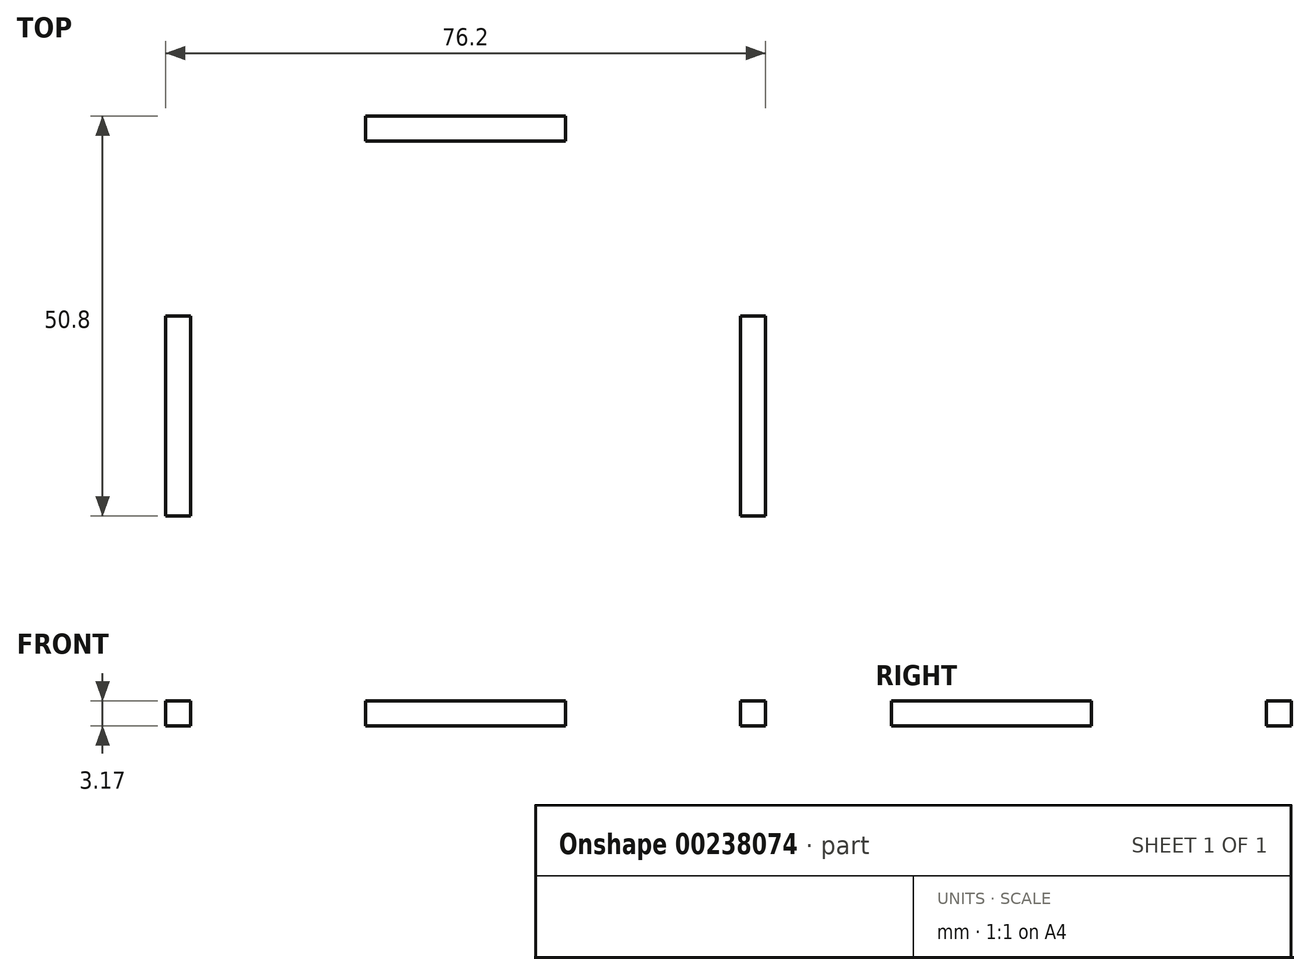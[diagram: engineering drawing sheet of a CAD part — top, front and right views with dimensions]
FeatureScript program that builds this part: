
annotation { "Feature Type Name" : "Feature", "Feature Type Description" : "" }
export const myFeature = defineFeature(function(context is Context, id is Id, definition is map)
    precondition{}
    {
        {
            var Q0;
            Q0=qCreatedBy(makeId("Top.planeOp"),FACE);
            var sketch = newSketch(context, id + "F0", { "sketchPlane" : qUnion([Q0])});
            skLineSegment(sketch, "E0.bottom", {"start": v(34.93, -34.93) * mm, "end": v(-34.93, -34.93) * mm});
            skLineSegment(sketch, "E0.top", {"start": v(34.93, 34.93) * mm, "end": v(-34.93, 34.93) * mm});
            skLineSegment(sketch, "E0.left", {"start": v(34.93, -34.93) * mm, "end": v(34.93, 34.92) * mm});
            skLineSegment(sketch, "E0.right", {"start": v(-34.93, -34.93) * mm, "end": v(-34.93, 34.92) * mm});
            skPoint(sketch, "E0.middle", {"position": v(0, 0) * mm});
            skLineSegment(sketch, "E1.bottom", {"start": v(-12.7, 38.1) * mm, "end": v(12.7, 38.1) * mm});
            skLineSegment(sketch, "E1.top", {"start": v(-12.7, 34.92) * mm, "end": v(12.7, 34.92) * mm});
            skLineSegment(sketch, "E1.left", {"start": v(-12.7, 38.1) * mm, "end": v(-12.7, 34.92) * mm});
            skLineSegment(sketch, "E1.right", {"start": v(12.7, 38.1) * mm, "end": v(12.7, 34.92) * mm});
            skLineSegment(sketch, "E2.bottom", {"start": v(-12.7, -34.93) * mm, "end": v(12.7, -34.93) * mm});
            skLineSegment(sketch, "E2.top", {"start": v(-12.7, -38.1) * mm, "end": v(12.7, -38.1) * mm});
            skLineSegment(sketch, "E2.left", {"start": v(-12.7, -34.93) * mm, "end": v(-12.7, -38.1) * mm});
            skLineSegment(sketch, "E2.right", {"start": v(12.7, -34.93) * mm, "end": v(12.7, -38.1) * mm});
            skLineSegment(sketch, "E3.bottom", {"start": v(34.93, 12.7) * mm, "end": v(38.1, 12.7) * mm});
            skLineSegment(sketch, "E3.top", {"start": v(34.93, -12.7) * mm, "end": v(38.1, -12.7) * mm});
            skLineSegment(sketch, "E3.left", {"start": v(34.93, 12.7) * mm, "end": v(34.93, -12.7) * mm});
            skLineSegment(sketch, "E3.right", {"start": v(38.1, 12.7) * mm, "end": v(38.1, -12.7) * mm});
            skLineSegment(sketch, "E4.bottom", {"start": v(-38.1, 12.7) * mm, "end": v(-34.93, 12.7) * mm});
            skLineSegment(sketch, "E4.top", {"start": v(-38.1, -12.7) * mm, "end": v(-34.93, -12.7) * mm});
            skLineSegment(sketch, "E4.left", {"start": v(-38.1, 12.7) * mm, "end": v(-38.1, -12.7) * mm});
            skLineSegment(sketch, "E4.right", {"start": v(-34.93, 12.7) * mm, "end": v(-34.93, -12.7) * mm});
            skLineSegment(sketch, "E5.bottom", {"start": v(-25.4, 17.46) * mm, "end": v(25.4, 17.46) * mm});
            skLineSegment(sketch, "E5.top", {"start": v(-25.4, 14.29) * mm, "end": v(25.4, 14.29) * mm});
            skLineSegment(sketch, "E5.left", {"start": v(-25.4, 17.46) * mm, "end": v(-25.4, 14.29) * mm});
            skLineSegment(sketch, "E5.right", {"start": v(25.4, 17.46) * mm, "end": v(25.4, 14.29) * mm});
            skLineSegment(sketch, "E6.bottom", {"start": v(-25.4, 1.59) * mm, "end": v(25.4, 1.59) * mm});
            skLineSegment(sketch, "E6.top", {"start": v(-25.4, -1.59) * mm, "end": v(25.4, -1.59) * mm});
            skLineSegment(sketch, "E6.left", {"start": v(-25.4, 1.59) * mm, "end": v(-25.4, -1.59) * mm});
            skLineSegment(sketch, "E6.right", {"start": v(25.4, 1.59) * mm, "end": v(25.4, -1.59) * mm});
            skLineSegment(sketch, "E7.bottom", {"start": v(-25.4, -14.29) * mm, "end": v(25.4, -14.29) * mm});
            skLineSegment(sketch, "E7.top", {"start": v(-25.4, -17.46) * mm, "end": v(25.4, -17.46) * mm});
            skLineSegment(sketch, "E7.left", {"start": v(-25.4, -14.29) * mm, "end": v(-25.4, -17.46) * mm});
            skLineSegment(sketch, "E7.right", {"start": v(25.4, -14.29) * mm, "end": v(25.4, -17.46) * mm});
            skLineSegment(sketch, "E8.bottom", {"start": v(-20.32, 14.29) * mm, "end": v(-13.97, 14.29) * mm});
            skLineSegment(sketch, "E8.top", {"start": v(-20.32, 13.02) * mm, "end": v(-13.97, 13.02) * mm});
            skLineSegment(sketch, "E8.left", {"start": v(-20.32, 14.29) * mm, "end": v(-20.32, 13.02) * mm});
            skLineSegment(sketch, "E8.right", {"start": v(-13.97, 14.29) * mm, "end": v(-13.97, 13.02) * mm});
            skLineSegment(sketch, "E9.bottom", {"start": v(-8.9, 14.29) * mm, "end": v(-2.54, 14.29) * mm});
            skLineSegment(sketch, "E9.top", {"start": v(-8.9, 13.02) * mm, "end": v(-2.54, 13.02) * mm});
            skLineSegment(sketch, "E9.left", {"start": v(-8.9, 14.29) * mm, "end": v(-8.9, 13.02) * mm});
            skLineSegment(sketch, "E9.right", {"start": v(-2.54, 14.29) * mm, "end": v(-2.54, 13.02) * mm});
            skLineSegment(sketch, "E10.bottom", {"start": v(2.54, 14.29) * mm, "end": v(8.89, 14.29) * mm});
            skLineSegment(sketch, "E10.top", {"start": v(2.54, 13.02) * mm, "end": v(8.89, 13.02) * mm});
            skLineSegment(sketch, "E10.left", {"start": v(2.54, 14.29) * mm, "end": v(2.54, 13.02) * mm});
            skLineSegment(sketch, "E10.right", {"start": v(8.89, 14.29) * mm, "end": v(8.89, 13.02) * mm});
            skLineSegment(sketch, "E11.bottom", {"start": v(13.97, 14.29) * mm, "end": v(20.32, 14.29) * mm});
            skLineSegment(sketch, "E11.top", {"start": v(13.97, 13.02) * mm, "end": v(20.32, 13.02) * mm});
            skLineSegment(sketch, "E11.left", {"start": v(13.97, 14.29) * mm, "end": v(13.97, 13.02) * mm});
            skLineSegment(sketch, "E11.right", {"start": v(20.32, 14.29) * mm, "end": v(20.32, 13.02) * mm});
            skLineSegment(sketch, "E12.bottom", {"start": v(-20.32, -1.59) * mm, "end": v(-13.97, -1.59) * mm});
            skLineSegment(sketch, "E12.top", {"start": v(-20.32, -2.86) * mm, "end": v(-13.97, -2.86) * mm});
            skLineSegment(sketch, "E12.left", {"start": v(-20.32, -1.59) * mm, "end": v(-20.32, -2.86) * mm});
            skLineSegment(sketch, "E12.right", {"start": v(-13.97, -1.59) * mm, "end": v(-13.97, -2.86) * mm});
            skLineSegment(sketch, "E13.bottom", {"start": v(-8.9, -1.59) * mm, "end": v(-2.54, -1.59) * mm});
            skLineSegment(sketch, "E13.top", {"start": v(-8.9, -2.86) * mm, "end": v(-2.54, -2.86) * mm});
            skLineSegment(sketch, "E13.left", {"start": v(-8.9, -1.59) * mm, "end": v(-8.9, -2.86) * mm});
            skLineSegment(sketch, "E13.right", {"start": v(-2.54, -1.59) * mm, "end": v(-2.54, -2.86) * mm});
            skLineSegment(sketch, "E14.bottom", {"start": v(2.54, -1.59) * mm, "end": v(8.89, -1.59) * mm});
            skLineSegment(sketch, "E14.top", {"start": v(2.54, -2.86) * mm, "end": v(8.89, -2.86) * mm});
            skLineSegment(sketch, "E14.left", {"start": v(2.54, -1.59) * mm, "end": v(2.54, -2.86) * mm});
            skLineSegment(sketch, "E14.right", {"start": v(8.89, -1.59) * mm, "end": v(8.89, -2.86) * mm});
            skLineSegment(sketch, "E15.bottom", {"start": v(13.97, -1.59) * mm, "end": v(20.32, -1.59) * mm});
            skLineSegment(sketch, "E15.top", {"start": v(13.97, -2.86) * mm, "end": v(20.32, -2.86) * mm});
            skLineSegment(sketch, "E15.left", {"start": v(13.97, -1.59) * mm, "end": v(13.97, -2.86) * mm});
            skLineSegment(sketch, "E15.right", {"start": v(20.32, -1.59) * mm, "end": v(20.32, -2.86) * mm});
            skLineSegment(sketch, "E16.bottom", {"start": v(-20.32, -17.46) * mm, "end": v(-13.97, -17.46) * mm});
            skLineSegment(sketch, "E16.top", {"start": v(-20.32, -18.73) * mm, "end": v(-13.97, -18.73) * mm});
            skLineSegment(sketch, "E16.left", {"start": v(-20.32, -17.46) * mm, "end": v(-20.32, -18.73) * mm});
            skLineSegment(sketch, "E16.right", {"start": v(-13.97, -17.46) * mm, "end": v(-13.97, -18.73) * mm});
            skLineSegment(sketch, "E17.bottom", {"start": v(-8.9, -17.46) * mm, "end": v(-2.54, -17.46) * mm});
            skLineSegment(sketch, "E17.top", {"start": v(-8.9, -18.73) * mm, "end": v(-2.54, -18.73) * mm});
            skLineSegment(sketch, "E17.left", {"start": v(-8.9, -17.46) * mm, "end": v(-8.9, -18.73) * mm});
            skLineSegment(sketch, "E17.right", {"start": v(-2.54, -17.46) * mm, "end": v(-2.54, -18.73) * mm});
            skLineSegment(sketch, "E18.bottom", {"start": v(2.54, -17.46) * mm, "end": v(8.89, -17.46) * mm});
            skLineSegment(sketch, "E18.top", {"start": v(2.54, -18.73) * mm, "end": v(8.89, -18.73) * mm});
            skLineSegment(sketch, "E18.left", {"start": v(2.54, -17.46) * mm, "end": v(2.54, -18.73) * mm});
            skLineSegment(sketch, "E18.right", {"start": v(8.89, -17.46) * mm, "end": v(8.89, -18.73) * mm});
            skLineSegment(sketch, "E19.bottom", {"start": v(13.97, -17.46) * mm, "end": v(20.32, -17.46) * mm});
            skLineSegment(sketch, "E19.top", {"start": v(13.97, -18.73) * mm, "end": v(20.32, -18.73) * mm});
            skLineSegment(sketch, "E19.left", {"start": v(13.97, -17.46) * mm, "end": v(13.97, -18.73) * mm});
            skLineSegment(sketch, "E19.right", {"start": v(20.32, -17.46) * mm, "end": v(20.32, -18.73) * mm});
            skSolve(sketch);
        }
        {
            var Q0;
            {var subQ42=sQuery(id+"F0.wireOp",EDGE,"E1.top");Q0=makeQuery(id+"F0.imprint","IMPRINT",FACE,{"disambiguationData":[TD([[makeQuery(id+"F0.imprint","IMPRINT",EDGE,{"derivedFrom":subQ42}),-1.0]])]});}
            var Q1;
            Q1=makeQuery(id+"F0.imprint","IMPRINT",FACE,{"disambiguationData":[TD([[makeQuery(id+"F0.imprint","IMPRINT",EDGE,{"derivedFrom":sQuery(id+"F0.wireOp",EDGE,"E1.bottom")}),-1.0]])]});
            var Q2;
            Q2=makeQuery(id+"F0.imprint","IMPRINT",FACE,{"disambiguationData":[TD([[makeQuery(id+"F0.imprint","IMPRINT",EDGE,{"derivedFrom":sQuery(id+"F0.wireOp",EDGE,"E3.bottom")}),-1.0]])]});
            var Q3;
            Q3=makeQuery(id+"F0.imprint","IMPRINT",FACE,{"disambiguationData":[TD([[makeQuery(id+"F0.imprint","IMPRINT",EDGE,{"derivedFrom":sQuery(id+"F0.wireOp",EDGE,"E2.bottom")}),-1.0]])]});
            var Q4;
            Q4=makeQuery(id+"F0.imprint","IMPRINT",FACE,{"disambiguationData":[TD([[makeQuery(id+"F0.imprint","IMPRINT",EDGE,{"derivedFrom":sQuery(id+"F0.wireOp",EDGE,"E4.bottom")}),-1.0]])]});
            extrude(context, id + "F1", {"entities" : qUnion([Q0, Q1, Q2, Q3, Q4]), "depth" : 3.17 * mm});
        }
    });
